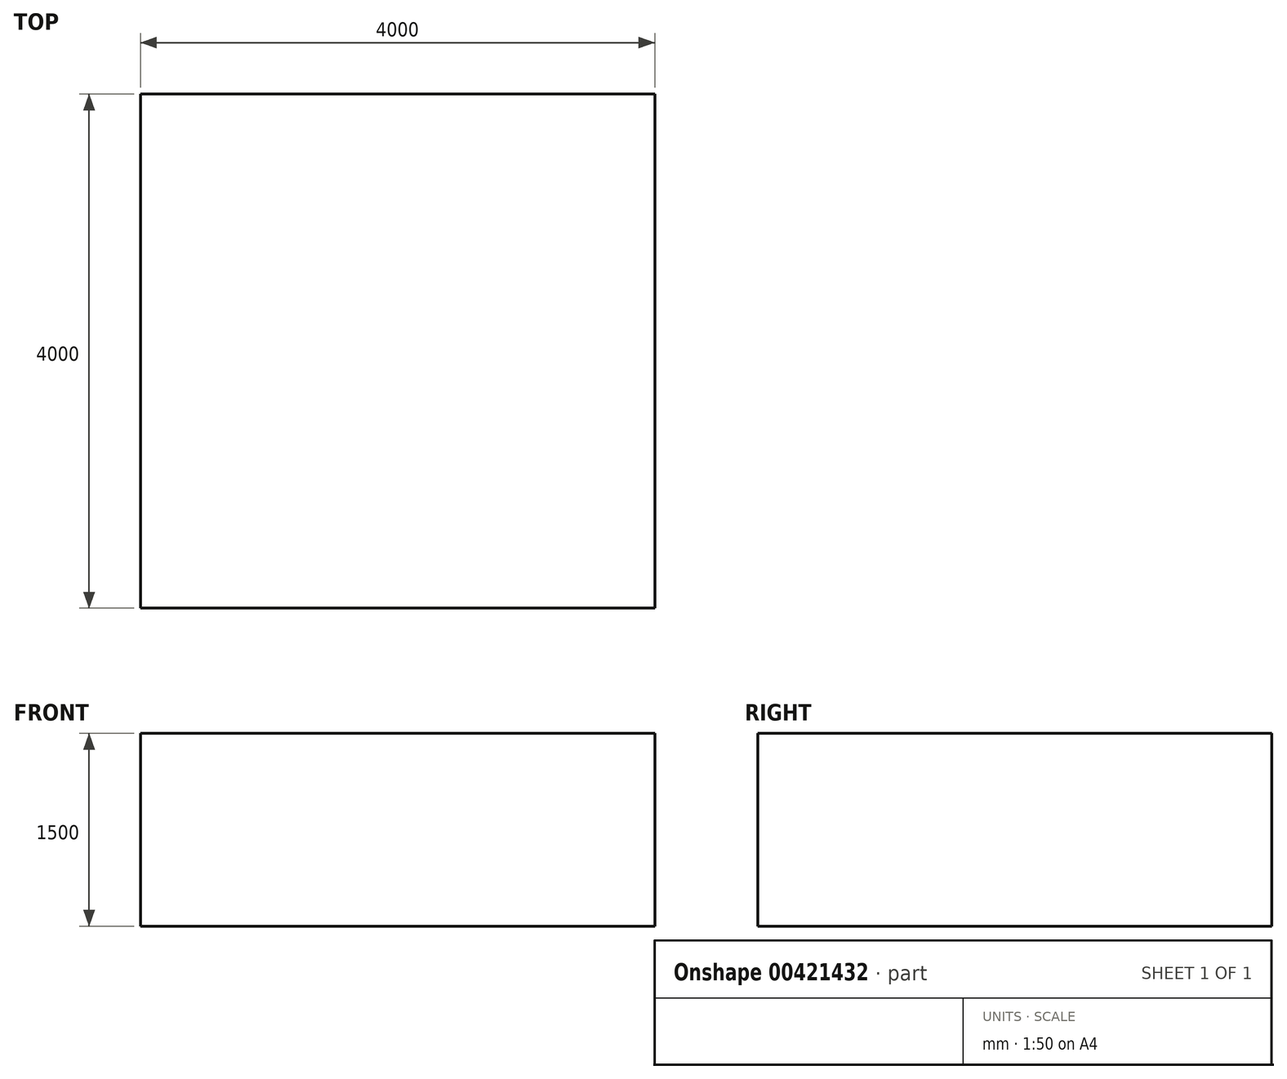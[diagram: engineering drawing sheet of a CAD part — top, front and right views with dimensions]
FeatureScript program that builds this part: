
annotation { "Feature Type Name" : "Feature", "Feature Type Description" : "" }
export const myFeature = defineFeature(function(context is Context, id is Id, definition is map)
    precondition{}
    {
        {
            var Q0;
            Q0=qCreatedBy(makeId("Top.planeOp"),FACE);
            var sketch = newSketch(context, id + "F0", { "sketchPlane" : qUnion([Q0])});
            skLineSegment(sketch, "E0.bottom", {"start": v(-2000, 2000) * mm, "end": v(2000, 2000) * mm});
            skLineSegment(sketch, "E0.top", {"start": v(-2000, -2000) * mm, "end": v(2000, -2000) * mm});
            skLineSegment(sketch, "E0.left", {"start": v(-2000, 2000) * mm, "end": v(-2000, -2000) * mm});
            skLineSegment(sketch, "E0.right", {"start": v(2000, 2000) * mm, "end": v(2000, -2000) * mm});
            skPoint(sketch, "E0.middle", {"position": v(0, 0) * mm});
            skSolve(sketch);
        }
        {
            var Q0;
            Q0 = qSketchRegion(id + "F0", true);
            extrude(context, id + "F1", {"entities" : qUnion([Q0]), "depth" : 1500 * mm});
        }
    });
